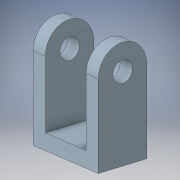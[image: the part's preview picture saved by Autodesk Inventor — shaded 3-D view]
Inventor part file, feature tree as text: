
AUTODESK INVENTOR PART (.ipt)
format: ipt  version: 2016 (Build 200138000, 138)  size: 130,560 bytes
history: native  units: mm
features: extrude x2, sketch x2, mirror x1, projected_geometry x1
ambient origin geometry x8: Origin, YZ Plane, XZ Plane, XY Plane, X Axis, Y Axis, Z Axis, Center Point
bodies: Solid1 (feature_tree)
feature tree (6):
  extrude  "Extrusion1"  Depth=80.0mm
  extrude  "Extrusion2"  Depth=50.0mm
  mirror  "Mirror1"
  sketch  "Sketch1"  dims[d0=50.0mm d1=80.0mm]
  sketch  "Sketch2"  dims[d2=15.0mm d3=0.0mm d5=50.0mm d6=20.0mm d7=80.0mm d8=50.0mm d9=15.0mm d10=0.0mm]
  projected_geometry  "Projected Loop1"
